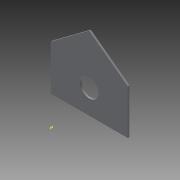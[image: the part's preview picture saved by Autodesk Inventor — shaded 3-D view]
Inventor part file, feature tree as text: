
AUTODESK INVENTOR PART (.ipt)
format: ipt  version: 2015 (Build 190159000, 159)  size: 122,368 bytes
history: native  units: in
note: dims shown in document units (in); Inventor stores cm internally (conversion verified against a paired STEP export)
features: sketch x11, extrude x6
ambient origin geometry x8: Origin, YZ Plane, XZ Plane, XY Plane, X Axis, Y Axis, Z Axis, Center Point
bodies: Solid1 (feature_tree)
feature tree (17):
  sketch  "Sketch1"  dims[d0=13.189in d1=17.7165in]
  extrude  "Extrusion1"  Depth=17.7165in
  extrude  "Extrusion2"  Depth=0.2756in TaperAngle=0.0deg
  extrude  "Extrusion3"  Depth=12.7953in
  sketch  "Sketch6"  dims[d11=12.0256in d12=0.0in d25=1.5748in]
  sketch  "Sketch7"  dims[d26=3.1496in d27=5.1181in]
  sketch  "Sketch8"  dims[d28=0.3937in d29=0.0in]
  sketch  "Sketch9"  dims[d30=2.5591in]
  extrude  "Extrusion6"  Depth=12.7953in
  extrude  "Extrusion7"  Depth=1.5748in
  extrude  "Extrusion8"  Depth=5.1181in
  sketch  "Sketch2"  dims[d2=6.5945in d3=0.2756in d4=0.0in]
  sketch  "Sketch3"  dims[d5=6.5945in d6=12.7953in]
  sketch  "Sketch5"  dims[d7=6.5369in d8=0.0in d10=12.7953in]
  sketch  "Sketch12"  dims[d31=1.5945in]
  sketch  "Sketch13"  dims[d32=1.5945in]
  sketch  "Sketch14"  dims[d33=0.3937in d34=0.0in d35=0.3937in d36=0.0in]
